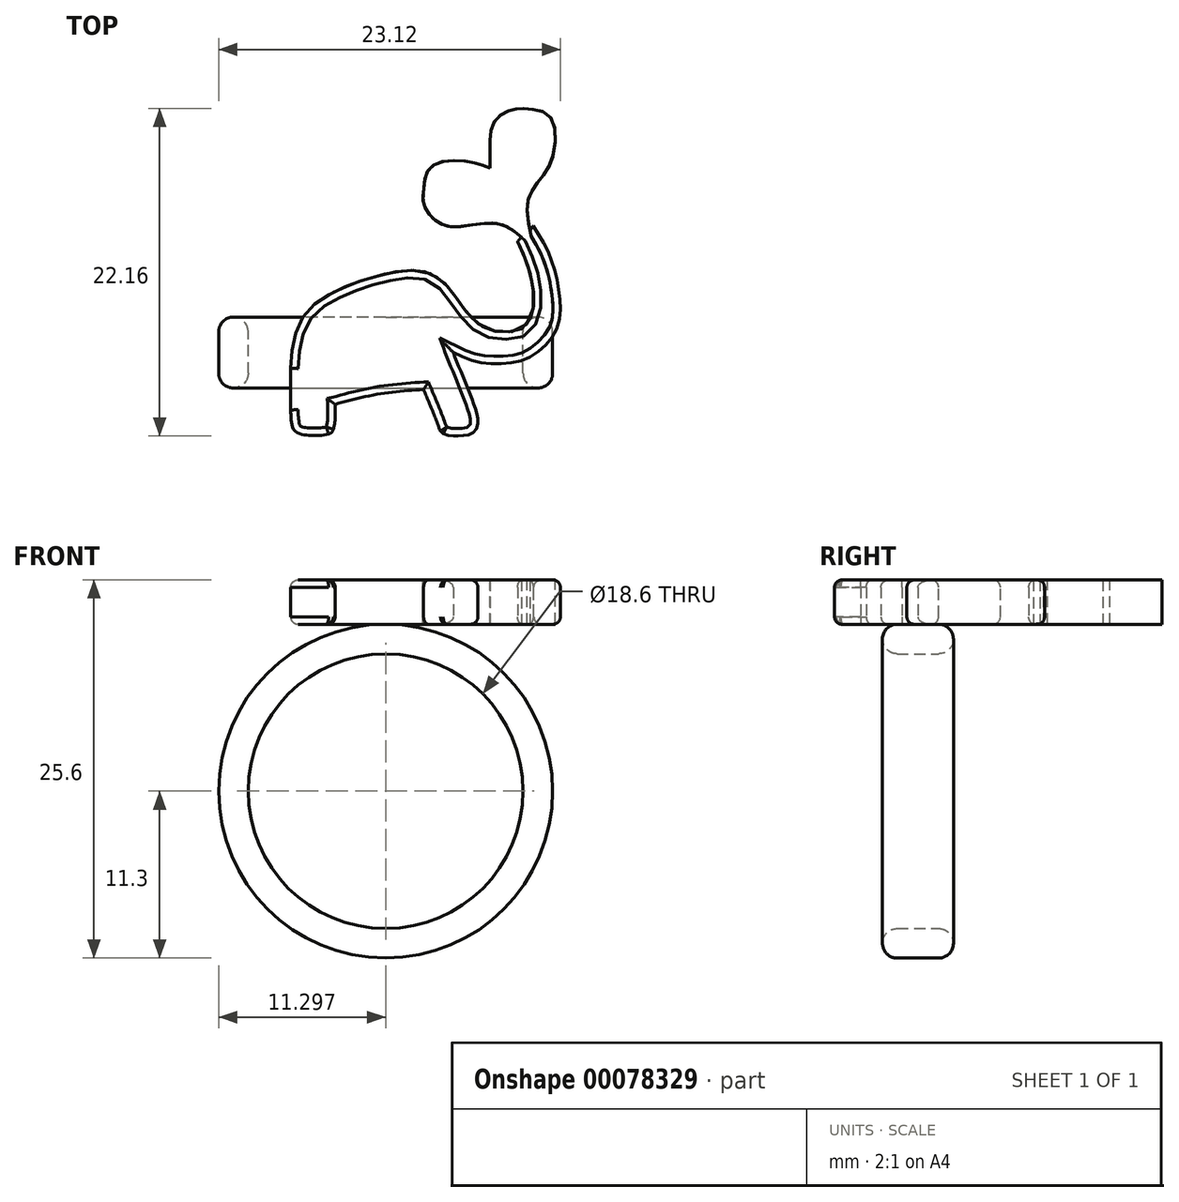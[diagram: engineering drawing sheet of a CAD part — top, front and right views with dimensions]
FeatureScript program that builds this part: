
annotation { "Feature Type Name" : "Feature", "Feature Type Description" : "" }
export const myFeature = defineFeature(function(context is Context, id is Id, definition is map)
    precondition{}
    {
        {
            var Q0;
            Q0=qCreatedBy(makeId("Top.planeOp"),FACE);
            var sketch = newSketch(context, id + "F0", { "sketchPlane" : qUnion([Q0])});
            skFitSpline(sketch, "E0", {"points": [v(-51.2, 9.9) * mm, v(-48.03, 10.62) * mm, v(-45.2, 10.9) * mm], "startDerivative": vector(6.19, 1.62) * mm, "endDerivative": vector(5.8, 0.37) * mm});
            skPoint(sketch, "E1", {"position": v(-51.2, 7.9) * mm});
            skFitSpline(sketch, "E2", {"points": [v(-51.2, 9.9) * mm, v(-51.2, 8.81) * mm, v(-51.32, 8.14) * mm, v(-51.58, 7.9) * mm, v(-53.57, 7.9) * mm, v(-54.06, 8.38) * mm, v(-54.2, 9.5) * mm], "startDerivative": vector(0.23, -6.22) * mm, "endDerivative": vector(-0.3, 6.77) * mm});
            skPoint(sketch, "E3", {"position": v(-54.2, 12.32) * mm});
            skLineSegment(sketch, "E4", {"start": v(-54.2, 12.32) * mm, "end": v(-54.2, 9.5) * mm});
            skPoint(sketch, "E5", {"position": v(-45.2, 18.9) * mm});
            skPoint(sketch, "E6", {"position": v(-43.2, 13.4) * mm});
            skPoint(sketch, "E7", {"position": v(-43.84, 7.9) * mm});
            skFitSpline(sketch, "E8", {"points": [v(-45.2, 10.9) * mm, v(-44.2, 8.44) * mm, v(-43.84, 7.9) * mm, v(-42.36, 7.79) * mm, v(-41.72, 8.07) * mm, v(-41.53, 8.87) * mm, v(-43.2, 13.4) * mm], "startDerivative": vector(5.53, -13.32) * mm, "endDerivative": vector(-7.08, 18.38) * mm});
            skPoint(sketch, "E9", {"position": v(-43.2, 17.4) * mm});
            skPoint(sketch, "E10", {"position": v(-38.84, 20.9) * mm});
            skFitSpline(sketch, "E11", {"points": [v(-54.2, 12.32) * mm, v(-52.95, 16.3) * mm, v(-47.4, 18.79) * mm, v(-45.2, 18.9) * mm, v(-44.08, 18.35) * mm, v(-43.2, 17.4) * mm, v(-42.32, 16.16) * mm, v(-41, 15.03) * mm, v(-39.64, 14.79) * mm, v(-38.57, 14.98) * mm, v(-37.98, 15.67) * mm, v(-37.74, 16.74) * mm, v(-38.03, 18.9) * mm, v(-38.84, 20.9) * mm], "startDerivative": vector(2.48, 38.08) * mm, "endDerivative": vector(-11.17, 23.46) * mm});
            skFitSpline(sketch, "E12", {"points": [v(-43.2, 13.4) * mm, v(-41.69, 12.79) * mm, v(-39.35, 12.69) * mm, v(-37.97, 13.1) * mm, v(-36.27, 14.79) * mm, v(-36, 17.27) * mm, v(-36.66, 19.96) * mm, v(-37.79, 21.96) * mm], "startDerivative": vector(11.3, -5.3) * mm, "endDerivative": vector(-8.8, 12.71) * mm});
            skPoint(sketch, "E13", {"position": v(-38.2, 29.9) * mm});
            skPoint(sketch, "E14", {"position": v(-40.7, 25.9) * mm});
            skPoint(sketch, "E15", {"position": v(-45.2, 24.4) * mm});
            skFitSpline(sketch, "E16", {"points": [v(-37.82, 20.56) * mm, v(-39.94, 22.07) * mm, v(-43, 21.9) * mm, v(-44.54, 22.45) * mm, v(-45.2, 23.5) * mm, v(-45.2, 24.4) * mm, v(-44.7, 25.96) * mm, v(-42.35, 26.34) * mm, v(-40.7, 25.9) * mm], "startDerivative": vector(-11.71, 7.66) * mm, "endDerivative": vector(11.9, -4.33) * mm});
            skFitSpline(sketch, "E17", {"points": [v(-40.7, 25.9) * mm, v(-40.7, 27.4) * mm, v(-40.42, 29) * mm, v(-39.28, 29.82) * mm, v(-38.2, 29.9) * mm, v(-36.6, 29.3) * mm, v(-36.56, 26.34) * mm, v(-37.49, 24.89) * mm, v(-38.2, 23.3) * mm, v(-37.82, 20.56) * mm], "startDerivative": vector(-0.02, 14.1) * mm, "endDerivative": vector(1.19, -16.95) * mm});
            skPoint(sketch, "E18", {"position": v(-47.86, 14.86) * mm});
            skLineSegment(sketch, "E19", {"start": v(-38.84, 20.9) * mm, "end": v(-38.59, 21.2) * mm});
            skLineSegment(sketch, "E20", {"start": v(-37.79, 21.96) * mm, "end": v(-38, 21.64) * mm});
            skSolve(sketch);
        }
        {
            var Q0;
            Q0 = qSketchRegion(id + "F0", true);
            extrude(context, id + "F1", {"entities" : qUnion([Q0]), "depth" : 3 * mm});
        }
        {
            var Q0;
            Q0=makeQuery(id+"F1.opExtrude","CAP_EDGE",EDGE,{"disambiguationData":[OSD([sQuery(id+"F0.wireOp",EDGE,"E11")])],"isStart":false});
            var Q1;
            Q1=makeQuery(id+"F1.opExtrude","CAP_EDGE",EDGE,{"disambiguationData":[OSD([sQuery(id+"F0.wireOp",EDGE,"E4")])],"isStart":false});
            var Q2;
            Q2=makeQuery(id+"F1.opExtrude","CAP_EDGE",EDGE,{"disambiguationData":[OSD([sQuery(id+"F0.wireOp",EDGE,"E2")])],"isStart":false});
            var Q3;
            Q3=makeQuery(id+"F1.opExtrude","CAP_EDGE",EDGE,{"disambiguationData":[OSD([sQuery(id+"F0.wireOp",EDGE,"E0")])],"isStart":false});
            var Q4;
            Q4=makeQuery(id+"F1.opExtrude","CAP_EDGE",EDGE,{"disambiguationData":[OSD([sQuery(id+"F0.wireOp",EDGE,"E8")])],"isStart":false});
            var Q5;
            Q5=makeQuery(id+"F1.opExtrude","CAP_EDGE",EDGE,{"disambiguationData":[OSD([sQuery(id+"F0.wireOp",EDGE,"E12")])],"isStart":false});
            fillet(context, id + "F2", {"entities" : qUnion([Q0, Q1, Q2, Q3, Q4, Q5]), "radius" : 0.5 * mm, "tangentPropagation" : true, "allowEdgeOverflow" : false});
        }
        {
            var Q0;
            Q0=makeQuery(id+"F1.opExtrude","CAP_EDGE",EDGE,{"disambiguationData":[OSD([sQuery(id+"F0.wireOp",EDGE,"E12")])],"isStart":true});
            var Q1;
            Q1=makeQuery(id+"F1.opExtrude","CAP_EDGE",EDGE,{"disambiguationData":[OSD([sQuery(id+"F0.wireOp",EDGE,"E11")])],"isStart":true});
            var Q2;
            Q2=makeQuery(id+"F1.opExtrude","CAP_EDGE",EDGE,{"disambiguationData":[OSD([sQuery(id+"F0.wireOp",EDGE,"E4")])],"isStart":true});
            var Q3;
            Q3=makeQuery(id+"F1.opExtrude","CAP_EDGE",EDGE,{"disambiguationData":[OSD([sQuery(id+"F0.wireOp",EDGE,"E2")])],"isStart":true});
            var Q4;
            Q4=makeQuery(id+"F1.opExtrude","CAP_EDGE",EDGE,{"disambiguationData":[OSD([sQuery(id+"F0.wireOp",EDGE,"E0")])],"isStart":true});
            var Q5;
            Q5=makeQuery(id+"F1.opExtrude","CAP_EDGE",EDGE,{"disambiguationData":[OSD([sQuery(id+"F0.wireOp",EDGE,"E8")])],"isStart":true});
            fillet(context, id + "F3", {"entities" : qUnion([Q0, Q1, Q2, Q3, Q4, Q5]), "radius" : 0.5 * mm, "tangentPropagation" : true, "allowEdgeOverflow" : false});
        }
        {
            var Q0;
            Q0=qCreatedBy(makeId("Right.planeOp"),FACE);
            cPlane(context, id + "F4", {"entities" : qUnion([Q0]), "cplaneType" : CPlaneType.OFFSET, "offset" : 47.76 * mm, "oppositeDirection" : true, "width" : 150 * mm, "height" : 150 * mm});
        }
        {
            var Q0;
            Q0=qCreatedBy(id+"F4.planeOp",FACE);
            var sketch = newSketch(context, id + "F5", { "sketchPlane" : qUnion([Q0])});
            skLineSegment(sketch, "E21", {"start": v(13.33, 3.24) * mm, "end": v(13.33, -23.2) * mm});
            skLineSegment(sketch, "E22", {"start": v(15.8, 0) * mm, "end": v(11, 0) * mm});
            skLineSegment(sketch, "E23", {"start": v(11, 0) * mm, "end": v(11, -2) * mm});
            skLineSegment(sketch, "E24", {"start": v(11, -2) * mm, "end": v(15.8, -2) * mm});
            skLineSegment(sketch, "E25", {"start": v(15.8, -2) * mm, "end": v(15.8, 0) * mm});
            skLineSegment(sketch, "E26", {"start": v(17.72, -11.3) * mm, "end": v(7.5, -11.3) * mm, "construction": true});
            skSolve(sketch);
        }
        {
            var Q0;
            Q0 = qSketchRegion(id + "F5", true);
            var Q1;
            Q1=sQuery(id+"F5.wireOp",EDGE,"E26");
            revolve(context, id + "F6", {"operationType" : NewBodyOperationType.ADD, "entities" : qUnion([Q0]), "axis" : qUnion([Q1]), "revolveType" : RevolveType.FULL});
        }
        {
            var Q0;
            Q0=makeQuery(id+"F6.opRevolve","SWEPT_EDGE",EDGE,{"disambiguationData":[OSD([sQuery(id+"F5.wireOp",EDGE,"E23"),sQuery(id+"F5.wireOp",EDGE,"E24")])]});
            var Q1;
            Q1=makeQuery(id+"F6.opRevolve","SWEPT_EDGE",EDGE,{"disambiguationData":[OSD([sQuery(id+"F5.wireOp",EDGE,"E24"),sQuery(id+"F5.wireOp",EDGE,"E25")])]});
            fillet(context, id + "F7", {"entities" : qUnion([Q0, Q1]), "radius" : 1 * mm, "tangentPropagation" : true, "allowEdgeOverflow" : false});
        }
        {
            var Q0;
            Q0=makeQuery(id+"F6.opRevolve","SWEPT_EDGE",EDGE,{"disambiguationData":[OSD([sQuery(id+"F5.wireOp",EDGE,"E22"),sQuery(id+"F5.wireOp",EDGE,"E23")])]});
            var Q1;
            Q1=makeQuery(id+"F6.opRevolve","SWEPT_EDGE",EDGE,{"disambiguationData":[OSD([sQuery(id+"F5.wireOp",EDGE,"E22"),sQuery(id+"F5.wireOp",EDGE,"E25")])]});
            fillet(context, id + "F8", {"entities" : qUnion([Q0, Q1]), "radius" : 1 * mm, "tangentPropagation" : true, "allowEdgeOverflow" : false});
        }
    });
